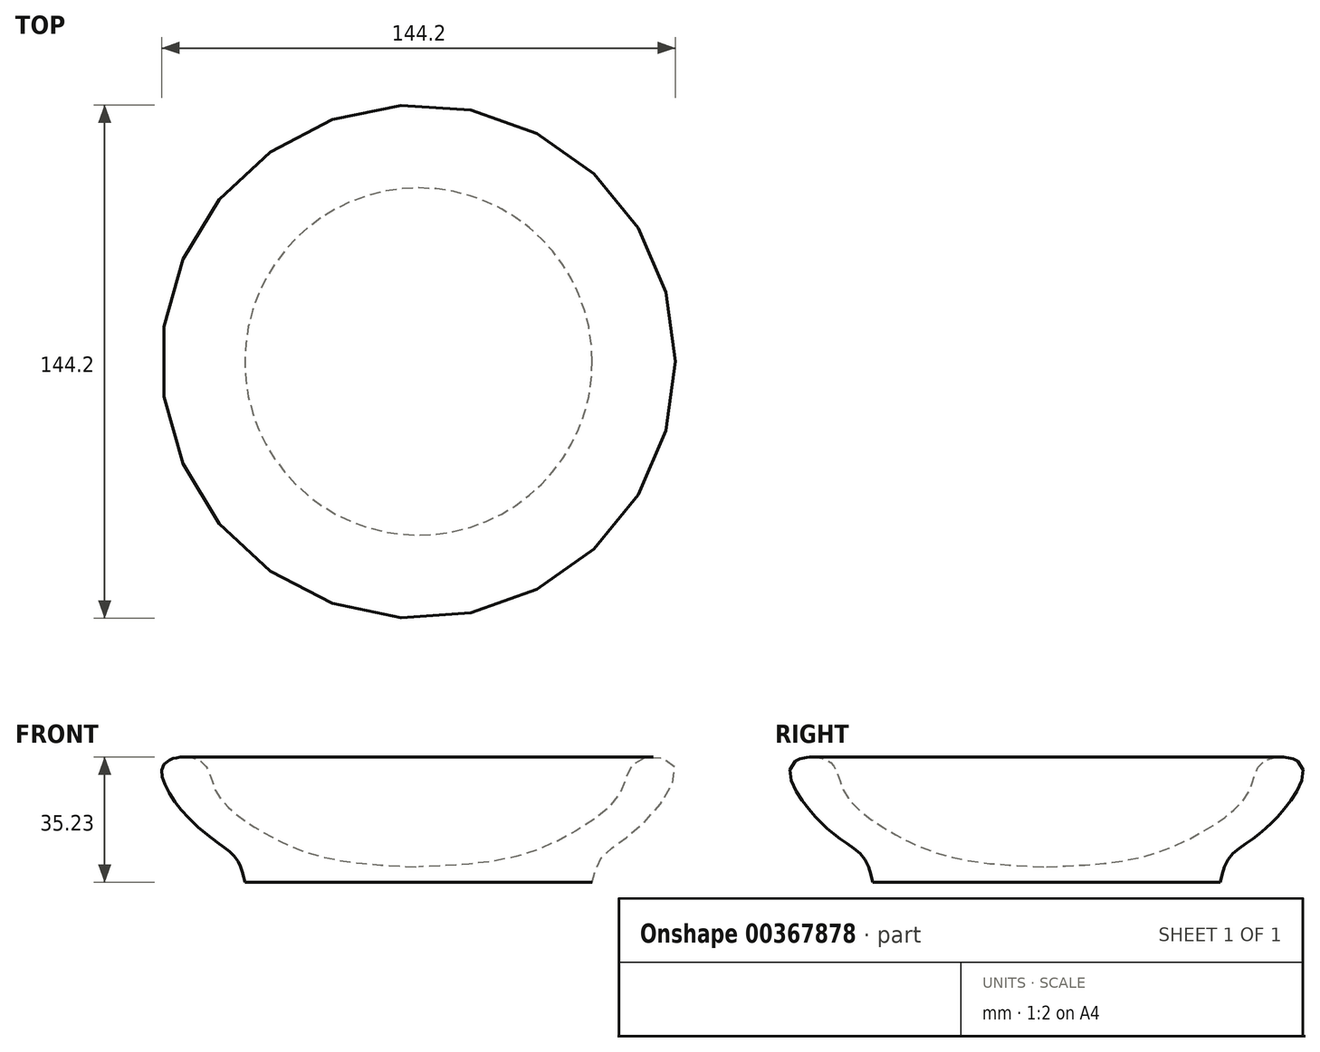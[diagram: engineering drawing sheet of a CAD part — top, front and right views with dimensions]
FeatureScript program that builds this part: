
annotation { "Feature Type Name" : "Feature", "Feature Type Description" : "" }
export const myFeature = defineFeature(function(context is Context, id is Id, definition is map)
    precondition{}
    {
        {
            var Q0;
            Q0=qCreatedBy(makeId("Front.planeOp"),FACE);
            var sketch = newSketch(context, id + "F0", { "sketchPlane" : qUnion([Q0])});
            skLineSegment(sketch, "E0", {"start": v(0, 4.4) * mm, "end": v(0, 0) * mm});
            skLineSegment(sketch, "E1", {"start": v(0, 0) * mm, "end": v(48.75, 0) * mm});
            skFitSpline(sketch, "E2", {"points": [v(48.75, 0) * mm, v(51.4, 7.05) * mm, v(62.26, 15.86) * mm, v(71.66, 32.9) * mm, v(61.09, 34.07) * mm, v(56.98, 25.85) * mm, v(45.52, 15.27) * mm, v(26.43, 7.05) * mm, v(0, 4.4) * mm], "startDerivative": vector(17.9, 84.84) * mm, "endDerivative": vector(-164.98, -6.26) * mm});
            skPoint(sketch, "E3.orphan", {"position": v(0, 43.76) * mm});
            skSolve(sketch);
        }
        {
            var Q0;
            Q0=makeQuery(id+"F0.imprint","IMPRINT",FACE,{"disambiguationData":[TD([[makeQuery(id+"F0.imprint","IMPRINT",EDGE,{"derivedFrom":sQuery(id+"F0.wireOp",EDGE,"E0")}),1.0]])]});
            var Q1;
            Q1=sQuery(id+"F0.wireOp",EDGE,"E0");
            revolve(context, id + "F1", {"entities" : qUnion([Q0]), "axis" : qUnion([Q1]), "revolveType" : RevolveType.FULL});
        }
    });
